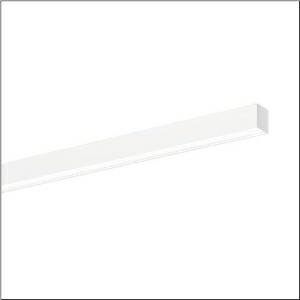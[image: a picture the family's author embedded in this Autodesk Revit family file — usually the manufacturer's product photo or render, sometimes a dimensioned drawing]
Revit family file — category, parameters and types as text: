
# Revit family: silica_21_51mx20tct5w
name_source: partatom
category: Lighting Fixtures
units: mm (PartAtom-declared; Revit-internal decimal feet)

## family parameters
Cut with Voids When Loaded = No
Host = Face
Light Source = No
Part Type = Normal
Room Calculation Point = No
Round Connector Dimension = Use Diameter
Shared = No

## types (1)
- --- (1 x LED, 6000 lm, 51.3 W, 6500K)
    Apparent Load = 51 VA
    CIE Flux Codes = 48 79 96 100 100
    Color Rendering = 80
    Color Temperature = 6500K
    Default Elevation = 1800 mm
    Description = Silica 21, office luminaire, primary optical cover: cover, of PMMA, opal, light emission: direct distribution, primary light characteristic: symmetric, installation type: surface-mounted, LED, rated luminous flux: 6.000lm, luminous efficacy: 112lm/W, light colour: 8tw, colour temperature: 2700..6500K, control gear: DALI DT8, with terminal, 3+2-pole, max. 2.5mm², mains connection: 220..240V, AC, 50/60Hz, rated input power: 53.8W, luminaire housing, of aluminium, traffic white (RAL 9016), length: 3.004mm, width: 53mm, height: 53mm, protection rating (complete): IP20, insulation class (complete): insulation class I (protective earthing), certification: CE, permissible operating ambient temperature: 0..+35°C, standard: EN 50419, packaging unit: 1 piece
    Height = 53 mm
    Lamp = 1 x LED
    Lamp Light Flux = 6000 lm
    Lamp Power = 51.3 W
    Lamp count = 1
    Length = 3004 mm
    Luminous efficacy = 117 lm/W
    Manufacturer = Siteco
    ModVariant = No
    Model = 51MX20TCT5W
    Mounting Place = Ceiling
    Mounting Type = Surface mounted
    Number of Poles = 1
    OnlyDefault = Yes
    Power Factor = 1
    Product Name = Silica 21
    Product group = office luminaire | ceiling mounted
    ProductGroupID = 301
    Protection Class = Protection class I
    Protection Degree = IP 20
    RLX_Detail_Level = 1
    RLX_Emergency_Light_Flux = 0 lm
    RLX_Emergency_Type = 0
    RLX_Emergency_Type_DB = No
    RlxData = <blob elided: 20593 chars, md5=d3a10fe4>
    Socket = socket
    Standby Power = 0 W
    System Light Flux = 6000 lm
    System Power = 51 W
    Type Comments = individual setting
    Type Image = l_1335877.jpg
    URL = http://relux.com
    VarID = @adj_139193
    Voltage = 0 V
    Weight = 0.00 kg
    Width = 53 mm

## geometry (parser evidence)
native form markers: Blend x4, Sweep x11
no freeform markers — native parametric forms only
